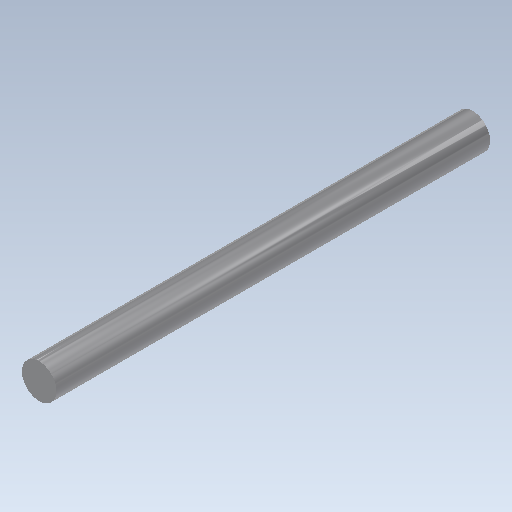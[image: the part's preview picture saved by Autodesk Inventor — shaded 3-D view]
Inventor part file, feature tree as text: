
AUTODESK INVENTOR PART (.ipt)
format: ipt  version: 2020 (Build 240168000, 168)  size: 94,720 bytes
history: native  units: mm
features: extrude x1, sketch x1
ambient origin geometry x8: Origin, YZ Plane, XZ Plane, XY Plane, X Axis, Y Axis, Z Axis, Center Point
bodies: Solid1 (feature_tree)
feature tree (2):
  extrude  "Extrusion1"  Depth=25.0mm TaperAngle=0.0deg
  sketch  "Sketch2"  dims[d0=2.0mm d1=25.0mm d2=0.0mm]
